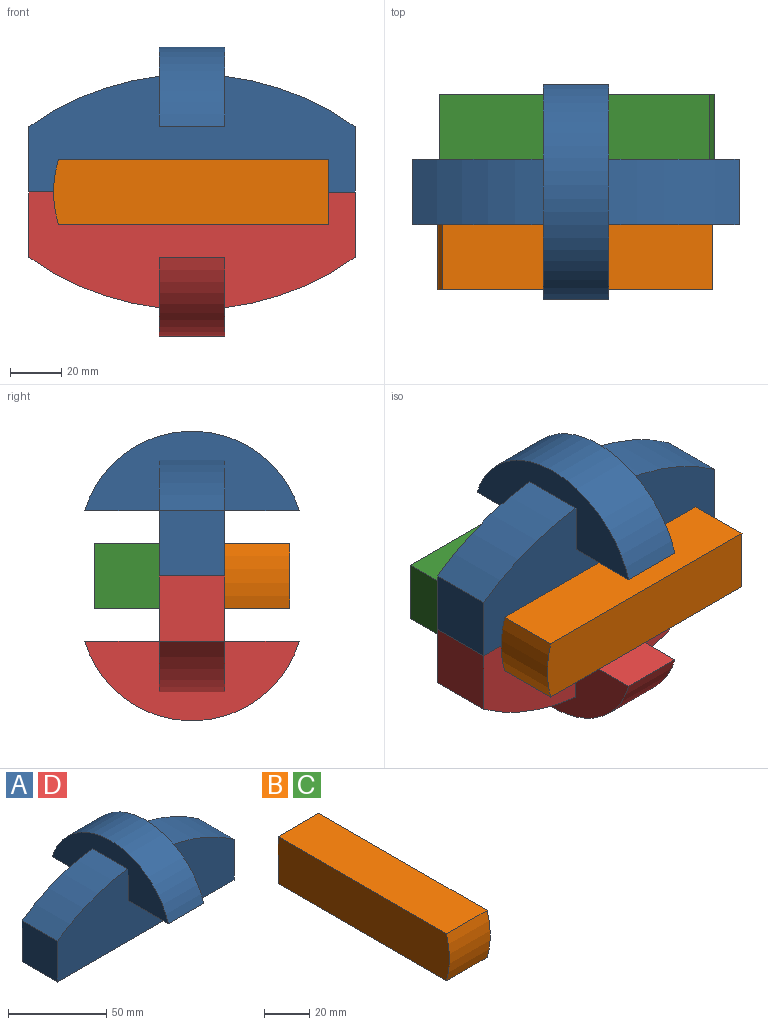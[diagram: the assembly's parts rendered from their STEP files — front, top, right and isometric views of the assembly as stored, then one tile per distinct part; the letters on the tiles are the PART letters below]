
ASSEMBLY  parts=4 mates=3
PART A: 12 faces, bbox 127x83.5x56.3 mm
  f0: cylinder r=109.07mm len=50.8mm, axis (0,1,0), area 1398.3mm2, adj f1,f4,f5,f11
  f1: plane 25.4x25.4mm, normal (-1,0,0), area 645.2mm2, adj f0,f2,f4,f5
  f2: plane 127x25.4mm, normal (0,0,-1), area 3225.8mm2, adj f1,f3,f4,f5
  f3: plane 25.4x25.4mm, normal (1,0,0), area 645.2mm2, adj f2,f4,f5,f6
  f4: plane 127x45.05mm, normal (0,-1,0), area 4475.6mm2, adj f0,f1,f2,f3,f6,f8,f10,f11
  f5: plane 127x45.05mm, normal (0,1,0), area 4475.6mm2, adj f0,f1,f2,f3,f6,f7,f10,f11
  f6: cylinder r=109.07mm len=50.8mm, axis (0,1,0), area 1398.3mm2, adj f3,f4,f5,f10
  f7: plane 29.06x25.4mm, normal (0,0,-1), area 738.1mm2, adj f5,f9,f10,f11
  f8: plane 29.06x25.4mm, normal (0,0,-1), area 738.1mm2, adj f4,f9,f10,f11
  f9: cylinder r=43.65mm len=83.52mm, axis (-1,0,0), area 2828.3mm2, adj f7,f8,f10,f11
  f10: plane 83.52x30.95mm, normal (1,0,0), area 1400.6mm2, adj f4,f5,f6,f7,f8,f9
  f11: plane 83.52x30.95mm, normal (-1,0,0), area 1400.6mm2, adj f0,f4,f5,f7,f8,f9
PART B: 6 faces, bbox 25.4x107.1x25.4 mm
  f0: plane 105.26x25.4mm, normal (0,0,1), area 2673.6mm2, adj f1,f3,f4,f5
  f1: cylinder r=43.65mm len=25.4mm, axis (-1,0,0), area 654.6mm2, adj f0,f2,f3,f4
  f2: plane 105.26x25.4mm, normal (0,0,-1), area 2673.6mm2, adj f1,f3,f4,f5
  f3: plane 107.15x25.4mm, normal (1,0,0), area 2705.7mm2, adj f0,f1,f2,f5
  f4: plane 107.15x25.4mm, normal (-1,0,0), area 2705.7mm2, adj f0,f1,f2,f5
  f5: plane 25.4x25.4mm, normal (0,1,0), area 645.2mm2, adj f0,f2,f3,f4
PART C: same geometry as B
PART D: same geometry as A
PLACE A t=(5,-1.82,-59.11)mm
PLACE B rot(axis=(-0.71,-0.71,0),180deg) t=(-5.24,-27.22,-71.81)mm
PLACE C rot(axis=(0,0,1),90deg) t=(15.23,23.58,-71.81)mm
PLACE D rot(axis=(-1,0,0),180deg) t=(5,-1.82,-84.51)mm
MATE fastened C.f4 <-> A.f5  axis (0,-1,0) through (5,10.88,-71.81)mm
MATE fastened B.f3 <-> A.f4  axis (0,1,0) through (5,-14.52,-71.81)mm
MATE fastened D.f2 <-> A.f2  axis (0,0,1) through (5,-1.82,-71.81)mm
